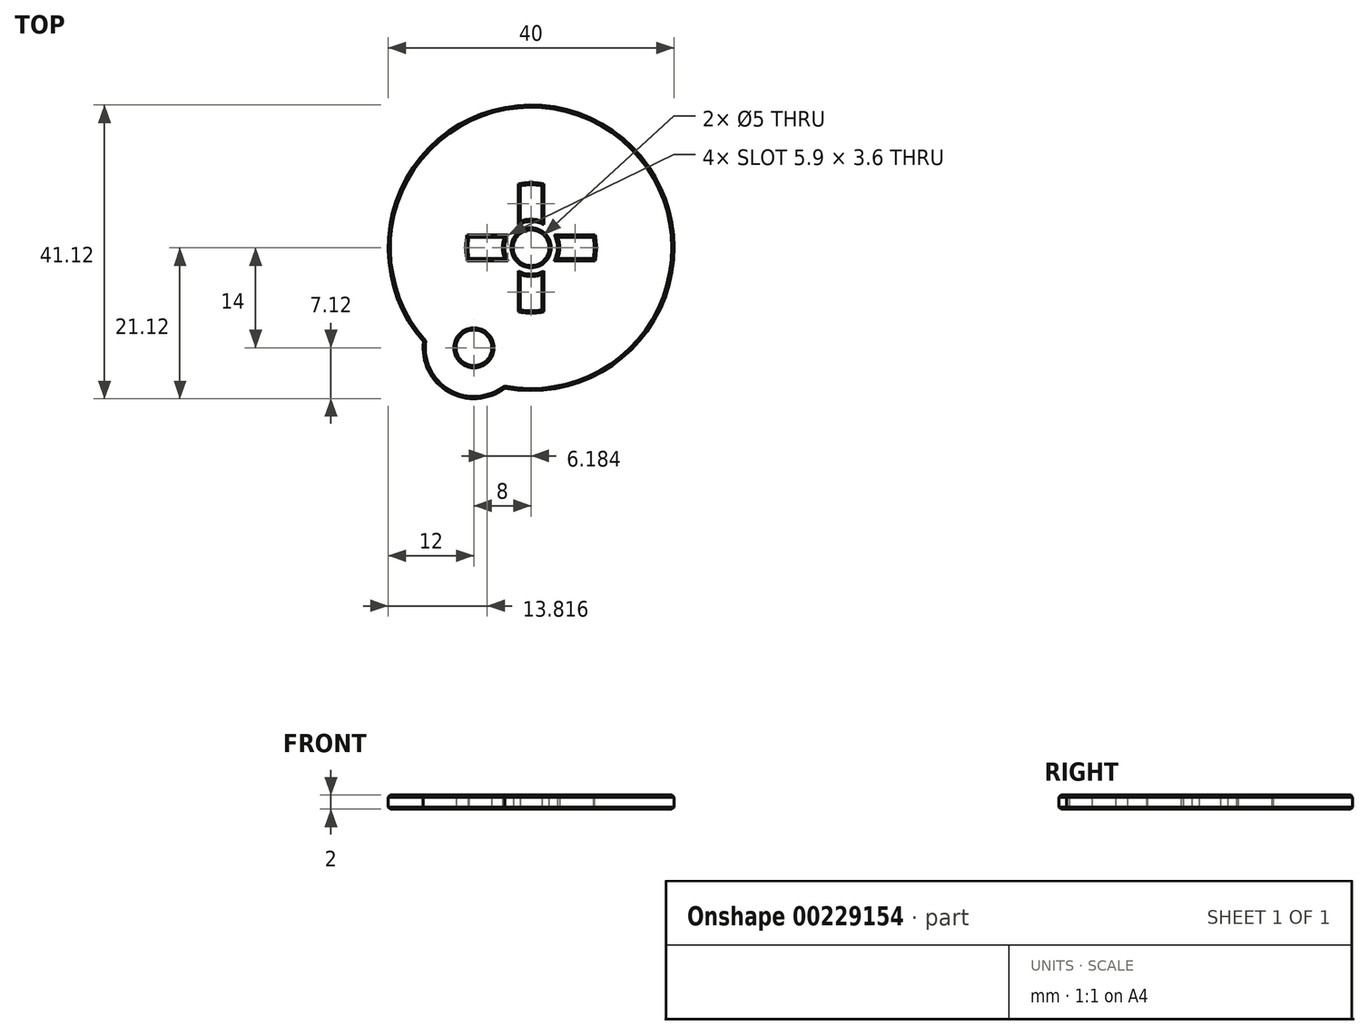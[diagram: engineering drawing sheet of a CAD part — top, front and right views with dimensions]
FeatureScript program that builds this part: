
annotation { "Feature Type Name" : "Feature", "Feature Type Description" : "" }
export const myFeature = defineFeature(function(context is Context, id is Id, definition is map)
    precondition{}
    {
        {
            var Q0;
            Q0=qCreatedBy(makeId("Top.planeOp"),FACE);
            var sketch = newSketch(context, id + "F0", { "sketchPlane" : qUnion([Q0])});
            skCircle(sketch, "E0", {"center": v(0, 0) * mm, "radius": 20 * mm});
            skLineSegment(sketch, "E1", {"start": v(-21.83, -14) * mm, "end": v(28.19, -14) * mm, "construction": true});
            skLineSegment(sketch, "E2", {"start": v(-8, 27.2) * mm, "end": v(-8, -24.35) * mm, "construction": true});
            skPoint(sketch, "E3", {"position": v(-8, -14) * mm});
            skLineSegment(sketch, "E4", {"start": v(-8.7, 1.5) * mm, "end": v(-3.7, 1.5) * mm});
            skLineSegment(sketch, "E5", {"start": v(-1.5, 8.7) * mm, "end": v(-1.5, 3.7) * mm});
            skLineSegment(sketch, "E6", {"start": v(-10.86, 0) * mm, "end": v(8.24, 0) * mm, "construction": true});
            skLineSegment(sketch, "E7", {"start": v(0, 8.22) * mm, "end": v(0, -5.08) * mm, "construction": true});
            skLineSegment(sketch, "E8.MirrorCS", {"start": v(1.5, 8.7) * mm, "end": v(1.5, 3.7) * mm});
            skLineSegment(sketch, "E9.MirrorCS", {"start": v(-8.7, -1.5) * mm, "end": v(-3.7, -1.5) * mm});
            skLineSegment(sketch, "E10.MirrorCS", {"start": v(8.7, -1.5) * mm, "end": v(3.7, -1.5) * mm});
            skLineSegment(sketch, "E11.MirrorCS", {"start": v(8.7, 1.5) * mm, "end": v(3.7, 1.5) * mm});
            skLineSegment(sketch, "E12.MirrorCS", {"start": v(1.5, -8.7) * mm, "end": v(1.5, -3.7) * mm});
            skLineSegment(sketch, "E13.MirrorCS", {"start": v(-1.5, -8.7) * mm, "end": v(-1.5, -3.7) * mm});
            skArc(sketch, "E14", {"start": v(-1.5, -3.7) * mm, "mid": v(0, -4) * mm, "end": v(1.5, -3.7) * mm});
            skCircle(sketch, "E15", {"center": v(0, 0) * mm, "radius": 2.5 * mm});
            skArc(sketch, "E16.trimOffspring", {"start": v(3.7, -1.5) * mm, "mid": v(4, 0) * mm, "end": v(3.7, 1.5) * mm});
            skArc(sketch, "E17.trimOffspring", {"start": v(1.5, 3.7) * mm, "mid": v(0, 4) * mm, "end": v(-1.5, 3.7) * mm});
            skArc(sketch, "E18.trimOffspring", {"start": v(-3.7, 1.5) * mm, "mid": v(-4, 0) * mm, "end": v(-3.7, -1.5) * mm});
            skArc(sketch, "E19", {"start": v(8.7, -1.5) * mm, "mid": v(8.84, 0) * mm, "end": v(8.7, 1.5) * mm});
            skArc(sketch, "E20.trimOffspring", {"start": v(-1.5, -8.7) * mm, "mid": v(0, -8.84) * mm, "end": v(1.5, -8.7) * mm});
            skArc(sketch, "E21.trimOffspring", {"start": v(-8.7, 1.5) * mm, "mid": v(-8.84, 0) * mm, "end": v(-8.7, -1.5) * mm});
            skArc(sketch, "E22.trimOffspring", {"start": v(1.5, 8.7) * mm, "mid": v(0, 8.84) * mm, "end": v(-1.5, 8.7) * mm});
            skSolve(sketch);
        }
        {
            var Q0;
            Q0 = qSketchRegion(id + "F0", true);
            extrude(context, id + "F1", {"entities" : qUnion([Q0]), "offsetDistance" : 25 * mm, "depth" : 2 * mm});
        }
        {
            var Q0;
            Q0=qCreatedBy(makeId("Top.planeOp"),FACE);
            var sketch = newSketch(context, id + "F2", { "sketchPlane" : qUnion([Q0])});
            skCircle(sketch, "E23", {"center": v(-8, -14) * mm, "radius": 7.12 * mm});
            skSolve(sketch);
        }
        {
            var Q0;
            Q0 = qSketchRegion(id + "F2", true);
            extrude(context, id + "F3", {"entities" : qUnion([Q0]), "operationType" : NewBodyOperationType.ADD, "depth" : 2 * mm, "offsetDistance" : 25 * mm});
        }
        {
            var Q0;
            Q0=sQuery(id+"F0.wireOp",VERTEX,"E3");
            var Q1;
            Q1=makeQuery(id+"F1.opExtrude","SWEPT_BODY",BODY,{"disambiguationData":[OSD([sQuery(id+"F0.wireOp",EDGE,"E0"),sQuery(id+"F0.wireOp",EDGE,"fWfHAkU1-x34K-Ojr9-oPNq-K8kwXMuBxkp4")])]});
            hole(context, id + "F4", {"style" : HoleStyle.SIMPLE, "endStyle" : HoleEndStyle.BLIND, "oppositeDirection" : true, "holeDiameter" : 5 * mm, "holeDepth" : 20.38 * mm, "tappedDepth" : 18 * mm, "tapClearance" : 3, "locations" : qUnion([Q0]), "scope" : qUnion([Q1])});
        }
        {
            var Q0;
            Q0=makeQuery(id+"F0.imprint","IMPRINT",FACE,{"disambiguationData":[TD([[makeQuery(id+"F0.imprint","IMPRINT",EDGE,{"derivedFrom":sQuery(id+"F0.wireOp",EDGE,"E0")}),1.0]])]});
            var sketch = newSketch(context, id + "F5", { "sketchPlane" : qUnion([Q0])});
            skCircle(sketch, "E24", {"center": v(0, 0) * mm, "radius": 10.5 * mm});
            skSolve(sketch);
        }
        {
            var Q0;
            Q0=makeQuery(id+"F1.opExtrude","CAP_FACE",FACE,{"disambiguationData":[OSD([sQuery(id+"F0.wireOp",EDGE,"E0"),sQuery(id+"F0.wireOp",EDGE,"fWfHAkU1-x34K-Ojr9-oPNq-K8kwXMuBxkp4")])],"isStart":false});
            var Q1;
            Q1=makeQuery(id+"F1.opExtrude","CAP_FACE",FACE,{"disambiguationData":[OSD([sQuery(id+"F0.wireOp",EDGE,"E0"),sQuery(id+"F0.wireOp",EDGE,"fWfHAkU1-x34K-Ojr9-oPNq-K8kwXMuBxkp4")])],"isStart":true});
            chamfer(context, id + "F6", {"entities" : qUnion([Q0, Q1]), "width" : .3 * mm, "tangentPropagation" : true});
        }
    });
